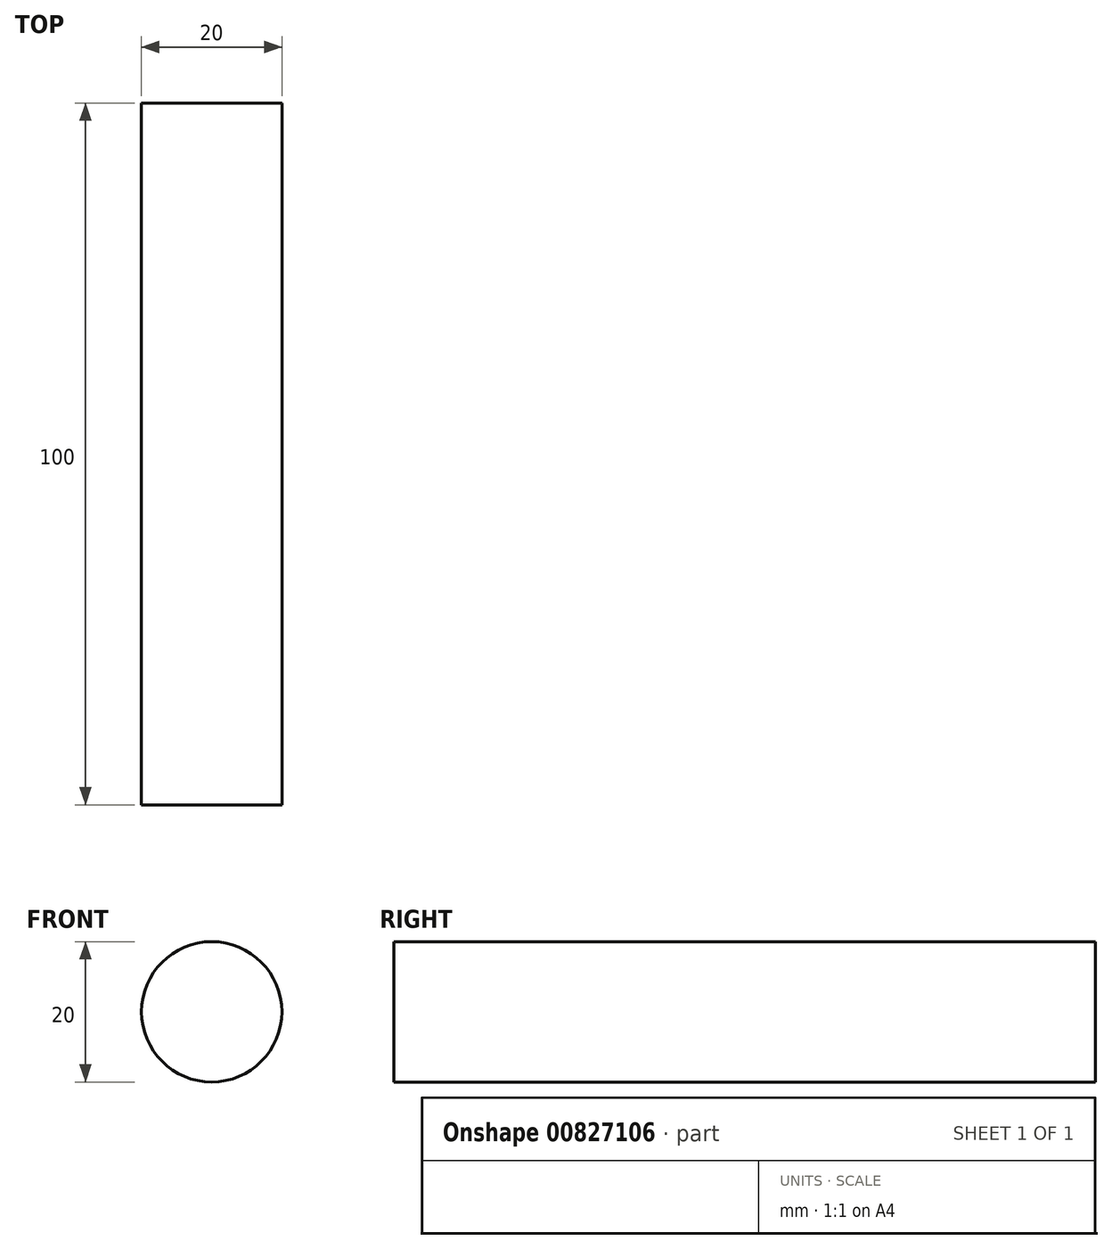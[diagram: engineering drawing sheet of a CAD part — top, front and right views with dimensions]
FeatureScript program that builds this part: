
annotation { "Feature Type Name" : "Feature", "Feature Type Description" : "" }
export const myFeature = defineFeature(function(context is Context, id is Id, definition is map)
    precondition{}
    {
        {
            var Q0;
            Q0=qCreatedBy(makeId("Front.planeOp"),FACE);
            var sketch = newSketch(context, id + "F0", { "sketchPlane" : qUnion([Q0])});
            skCircle(sketch, "E0", {"center": v(0, 0) * mm, "radius": 10 * mm});
            skSolve(sketch);
        }
        {
            var Q0;
            Q0=makeQuery(id+"F0.imprint","IMPRINT",FACE,{"disambiguationData":[TD([[makeQuery(id+"F0.imprint","IMPRINT",EDGE,{"derivedFrom":sQuery(id+"F0.wireOp",EDGE,"E0")}),1.0]])]});
            extrude(context, id + "F1", {"entities" : qUnion([Q0]), "depth" : 100 * mm, "offsetDistance" : 25 * mm});
        }
    });
